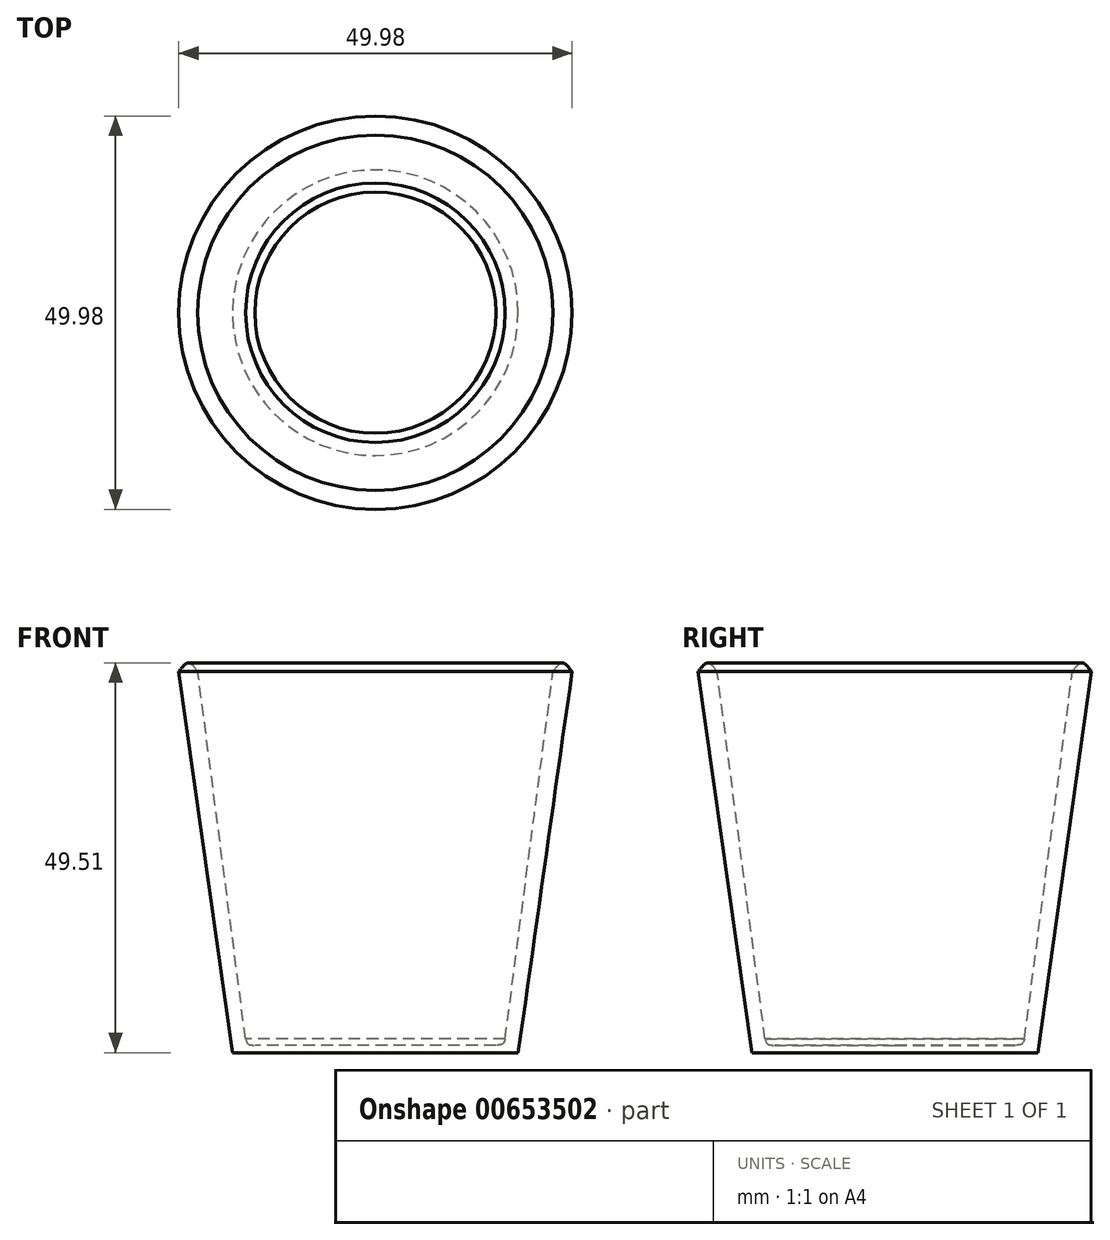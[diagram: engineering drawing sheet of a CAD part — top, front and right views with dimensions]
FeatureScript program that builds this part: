
annotation { "Feature Type Name" : "Feature", "Feature Type Description" : "" }
export const myFeature = defineFeature(function(context is Context, id is Id, definition is map)
    precondition{}
    {
        {
            var Q0;
            Q0=qCreatedBy(makeId("Front.planeOp"),FACE);
            var sketch = newSketch(context, id + "F0", { "sketchPlane" : qUnion([Q0])});
            skLineSegment(sketch, "E0", {"start": v(0, 3.58) * mm, "end": v(-18.15, 3.58) * mm});
            skLineSegment(sketch, "E1", {"start": v(-18.15, 3.58) * mm, "end": v(-24.99, 51.98) * mm});
            skFitSpline(sketch, "E2", {"points": [v(-24.99, 51.98) * mm, v(-22.56, 51.98) * mm], "startDerivative": vector(2.8, 3.47) * mm, "endDerivative": vector(3.6, -5.38) * mm});
            skLineSegment(sketch, "E3", {"start": v(-22.56, 51.98) * mm, "end": v(-16.48, 5.33) * mm});
            skFitSpline(sketch, "E4", {"points": [v(-16.48, 5.33) * mm, v(-15.31, 4.53) * mm], "startDerivative": vector(0.56, -2.56) * mm, "endDerivative": vector(1.65, -0.05) * mm});
            skLineSegment(sketch, "E5", {"start": v(-15.31, 4.53) * mm, "end": v(0, 4.53) * mm});
            skLineSegment(sketch, "E6", {"start": v(0, 4.53) * mm, "end": v(0, 3.58) * mm});
            skSolve(sketch);
        }
        {
            var Q0;
            Q0 = qSketchRegion(id + "F0", true);
            var Q1;
            Q1=sQuery(id+"F0.wireOp",EDGE,"E6");
            revolve(context, id + "F1", {"entities" : qUnion([Q0]), "axis" : qUnion([Q1]), "revolveType" : RevolveType.FULL});
        }
    });
